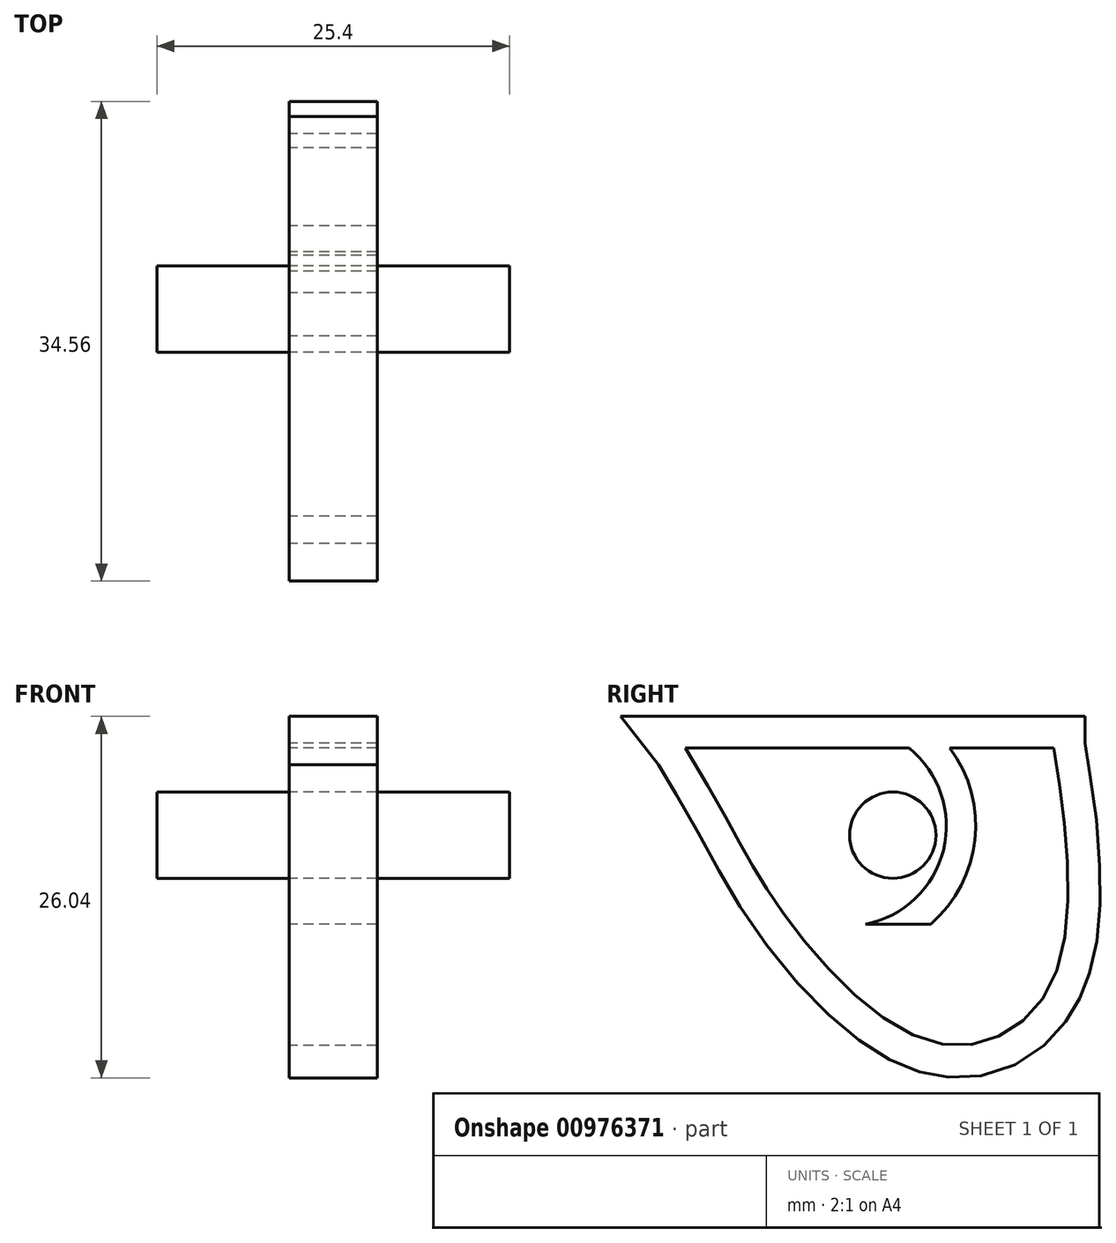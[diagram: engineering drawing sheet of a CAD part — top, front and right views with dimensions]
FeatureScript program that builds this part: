
annotation { "Feature Type Name" : "Feature", "Feature Type Description" : "" }
export const myFeature = defineFeature(function(context is Context, id is Id, definition is map)
    precondition{}
    {
        {
            var Q0;
            Q0=qCreatedBy(makeId("Right.planeOp"),FACE);
            var sketch = newSketch(context, id + "F0", { "sketchPlane" : qUnion([Q0])});
            skLineSegment(sketch, "E0", {"start": v(-30.76, 21.22) * mm, "end": v(-4.21, 21.22) * mm});
            skArc(sketch, "E1", {"start": v(-17.77, 8.53) * mm, "mid": v(-12.17, 13.88) * mm, "end": v(-14.64, 21.22) * mm});
            skLineSegment(sketch, "E2", {"start": v(-17.77, 8.53) * mm, "end": v(-12.64, 8.53) * mm});
            skPoint(sketch, "E2.endSnap0", {"position": v(-12.64, 12.55) * mm});
            skPoint(sketch, "E3.end.orphan", {"position": v(-12.64, 21.22) * mm});
            skArc(sketch, "E4.0", {"start": v(-13.1, 8.53) * mm, "mid": v(-9.9, 14.6) * mm, "end": v(-11.72, 21.22) * mm});
            skPoint(sketch, "E5.2.internal.orphan", {"position": v(-26.94, 0) * mm});
            skFitSpline(sketch, "E6", {"points": [v(-4.21, 21.22) * mm, v(-4.41, 4.24) * mm, v(-12.78, 0) * mm, v(-24.1, 9.9) * mm, v(-30.76, 21.22) * mm], "startDerivative": vector(8.9, -57.82) * mm, "endDerivative": vector(-42.9, 69.9) * mm});
            skPoint(sketch, "E7.orphan", {"position": v(0, 21.22) * mm});
            skLineSegment(sketch, "E8.0", {"start": v(-35.43, 23.5) * mm, "end": v(-1.95, 23.5) * mm});
            skFitSpline(sketch, "E9.0", {"points": [v(-1.95, 21.57) * mm, v(-1.77, 20.36) * mm, v(-1.37, 17.74) * mm, v(-0.98, 14.2) * mm, v(-0.87, 11.35) * mm, v(-0.92, 9.22) * mm, v(-1.15, 7.13) * mm, v(-1.52, 5.45) * mm, v(-1.95, 4.15) * mm, v(-2.36, 3.2) * mm, v(-2.85, 2.3) * mm, v(-3.6, 1.18) * mm, v(-4.72, -0.04) * mm, v(-6.3, -1.21) * mm, v(-8.07, -2.04) * mm, v(-9.99, -2.49) * mm, v(-11.66, -2.51) * mm, v(-13, -2.31) * mm, v(-14.34, -1.96) * mm, v(-15.92, -1.3) * mm, v(-17.68, -0.22) * mm, v(-19.34, 1.05) * mm, v(-21.4, 2.94) * mm, v(-23.72, 5.51) * mm, v(-25.99, 8.53) * mm, v(-27.6, 11.06) * mm, v(-28.94, 13.47) * mm, v(-30.43, 16.2) * mm, v(-31.83, 18.59) * mm, v(-32.7, 20.02) * mm]});
            skLineSegment(sketch, "E10", {"start": v(-1.95, 21.57) * mm, "end": v(-1.95, 23.5) * mm});
            skLineSegment(sketch, "E11", {"start": v(-32.7, 20.02) * mm, "end": v(-35.43, 23.5) * mm});
            skSolve(sketch);
        }
        {
            var Q0;
            Q0 = qSketchRegion(id + "F0", true);
            extrude(context, id + "F1", {"entities" : qUnion([Q0]), "endBound" : BoundingType.SYMMETRIC, "depth" : 6.35 * mm, "offsetDistance" : 25.4 * mm});
        }
        {
            var Q0;
            {var subQ0=sQuery(id+"F0.wireOp",EDGE,"E1");Q0=makeQuery(id+"F0.imprint","IMPRINT",FACE,{"disambiguationData":[TD([[makeQuery(id+"F0.imprint","IMPRINT",EDGE,{"derivedFrom":subQ0}),-1.0]])]});}
            extrude(context, id + "F2", {"entities" : qUnion([Q0]), "operationType" : NewBodyOperationType.ADD, "endBound" : BoundingType.SYMMETRIC, "depth" : 6.35 * mm, "offsetDistance" : 25.4 * mm});
        }
        {
            var Q0;
            Q0=qCreatedBy(makeId("Right.planeOp"),FACE);
            var sketch = newSketch(context, id + "F3", { "sketchPlane" : qUnion([Q0])});
            skCircle(sketch, "E12", {"center": v(-15.82, 14.95) * mm, "radius": 3.1 * mm});
            skSolve(sketch);
        }
        {
            var Q0;
            Q0 = qSketchRegion(id + "F3", true);
            extrude(context, id + "F4", {"entities" : qUnion([Q0]), "endBound" : BoundingType.SYMMETRIC, "depth" : 25.4 * mm, "offsetDistance" : 25.4 * mm});
        }
    });
